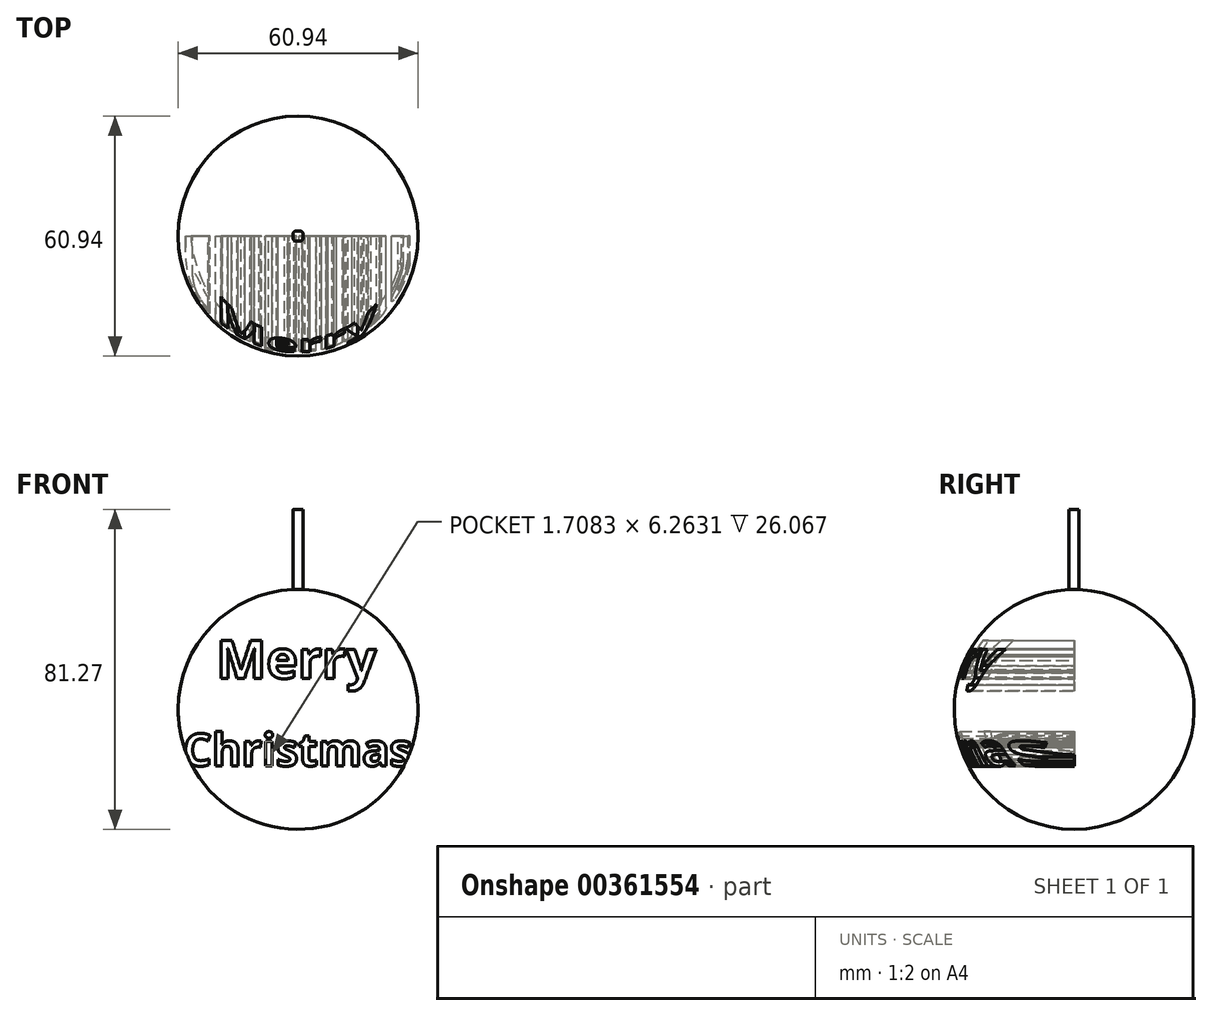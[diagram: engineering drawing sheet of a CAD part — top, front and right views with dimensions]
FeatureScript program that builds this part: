
annotation { "Feature Type Name" : "Feature", "Feature Type Description" : "" }
export const myFeature = defineFeature(function(context is Context, id is Id, definition is map)
    precondition{}
    {
        {
            var Q0;
            Q0=qCreatedBy(makeId("Front.planeOp"),FACE);
            var sketch = newSketch(context, id + "F0", { "sketchPlane" : qUnion([Q0])});
            skCircle(sketch, "E0", {"center": v(0, 0) * mm, "radius": 30.47 * mm});
            skLineSegment(sketch, "E1", {"start": v(-30.47, 0) * mm, "end": v(30.47, 0) * mm});
            skSolve(sketch);
        }
        {
            var Q0;
            {var subQ0=sQuery(id+"F0.wireOp",EDGE,"E1");Q0=makeQuery(id+"F0.imprint","IMPRINT",FACE,{"disambiguationData":[TD([[makeQuery(id+"F0.imprint","IMPRINT",EDGE,{"derivedFrom":subQ0}),-1.0]])]});}
            var Q1;
            Q1=sQuery(id+"F0.wireOp",EDGE,"E1");
            revolve(context, id + "F1", {"entities" : qUnion([Q0]), "axis" : qUnion([Q1]), "revolveType" : RevolveType.FULL});
        }
        {
            var Q0;
            Q0=qCreatedBy(makeId("Top.planeOp"),FACE);
            var sketch = newSketch(context, id + "F2", { "sketchPlane" : qUnion([Q0])});
            skLineSegment(sketch, "E2.bottom", {"start": v(-1.27, 1.27) * mm, "end": v(1.27, 1.27) * mm});
            skLineSegment(sketch, "E2.top", {"start": v(-1.27, -1.27) * mm, "end": v(1.27, -1.27) * mm});
            skLineSegment(sketch, "E2.left", {"start": v(-1.27, 1.27) * mm, "end": v(-1.27, -1.27) * mm});
            skLineSegment(sketch, "E2.right", {"start": v(1.27, 1.27) * mm, "end": v(1.27, -1.27) * mm});
            skSolve(sketch);
        }
        {
            var Q0;
            Q0 = qSketchRegion(id + "F2", true);
            extrude(context, id + "F3", {"entities" : qUnion([Q0]), "operationType" : NewBodyOperationType.ADD, "depth" : 50.8 * mm});
        }
        {
            var Q0;
            {var subQ0=sQuery(id+"F2.wireOp",EDGE,"E2.bottom");var subQ1=sQuery(id+"F2.wireOp",EDGE,"E2.left");Q0=makeQuery(id+"F3.boolean.opBoolean","SPLIT",EDGE,{"disambiguationData":[TD([makeQuery(id+"F3.opExtrude","CAP_FACE",FACE,{"disambiguationData":[OSD([subQ0,sQuery(id+"F2.wireOp",EDGE,"E2.top"),subQ1,sQuery(id+"F2.wireOp",EDGE,"E2.right")])],"isStart":true})])],"derivedFrom":makeQuery(id+"F3.opExtrude","SWEPT_EDGE",EDGE,{"disambiguationData":[OSD([subQ0,subQ1])]})});}
            var Q1;
            {var subQ0=sQuery(id+"F2.wireOp",EDGE,"E2.bottom");var subQ1=sQuery(id+"F2.wireOp",EDGE,"E2.right");Q1=makeQuery(id+"F3.boolean.opBoolean","SPLIT",EDGE,{"disambiguationData":[TD([makeQuery(id+"F3.opExtrude","CAP_FACE",FACE,{"disambiguationData":[OSD([subQ0,sQuery(id+"F2.wireOp",EDGE,"E2.top"),sQuery(id+"F2.wireOp",EDGE,"E2.left"),subQ1])],"isStart":true})])],"derivedFrom":makeQuery(id+"F3.opExtrude","SWEPT_EDGE",EDGE,{"disambiguationData":[OSD([subQ0,subQ1])]})});}
            var Q2;
            {var subQ0=sQuery(id+"F2.wireOp",EDGE,"E2.left");var subQ1=sQuery(id+"F2.wireOp",EDGE,"E2.top");Q2=makeQuery(id+"F3.boolean.opBoolean","SPLIT",EDGE,{"disambiguationData":[TD([makeQuery(id+"F3.opExtrude","CAP_FACE",FACE,{"disambiguationData":[OSD([sQuery(id+"F2.wireOp",EDGE,"E2.bottom"),subQ1,subQ0,sQuery(id+"F2.wireOp",EDGE,"E2.right")])],"isStart":true})])],"derivedFrom":makeQuery(id+"F3.opExtrude","SWEPT_EDGE",EDGE,{"disambiguationData":[OSD([subQ1,subQ0])]})});}
            var Q3;
            {var subQ0=sQuery(id+"F2.wireOp",EDGE,"E2.right");var subQ1=sQuery(id+"F2.wireOp",EDGE,"E2.top");Q3=makeQuery(id+"F3.boolean.opBoolean","SPLIT",EDGE,{"disambiguationData":[TD([makeQuery(id+"F3.opExtrude","CAP_FACE",FACE,{"disambiguationData":[OSD([sQuery(id+"F2.wireOp",EDGE,"E2.bottom"),subQ1,sQuery(id+"F2.wireOp",EDGE,"E2.left"),subQ0])],"isStart":true})])],"derivedFrom":makeQuery(id+"F3.opExtrude","SWEPT_EDGE",EDGE,{"disambiguationData":[OSD([subQ1,subQ0])]})});}
            fillet(context, id + "F4", {"entities" : qUnion([Q0, Q1, Q2, Q3]), "radius" : 0.76 * mm, "tangentPropagation" : true, "allowEdgeOverflow" : false});
        }
        {
            var Q0;
            Q0=qCreatedBy(makeId("Front.planeOp"),FACE);
            var sketch = newSketch(context, id + "F5", { "sketchPlane" : qUnion([Q0])});
            skText(sketch, "E3", { "text": "Merry", "fontName": "OpenSans-Bold.ttf"});
            const initialGuessF5  = {"E3": [-0.02078, 0.0079, 1, 0, 0.00973]};
            skSetInitialGuess(sketch, initialGuessF5);
            skSolve(sketch);
        }
        {
            var Q0;
            Q0 = qSketchRegion(id + "F5", true);
            extrude(context, id + "F6", {"entities" : qUnion([Q0]), "operationType" : NewBodyOperationType.REMOVE, "depth" : 127 * mm});
        }
        {
            var Q0;
            Q0=qCreatedBy(makeId("Front.planeOp"),FACE);
            var sketch = newSketch(context, id + "F7", { "sketchPlane" : qUnion([Q0])});
            skText(sketch, "E4", { "text": "Christmas", "fontName": "OpenSans-Bold.ttf"});
            const initialGuessF7  = {"E4": [-0.02921, -0.01435, 1, 0, 0.00826]};
            skSetInitialGuess(sketch, initialGuessF7);
            skSolve(sketch);
        }
        {
            var Q0;
            Q0 = qSketchRegion(id + "F7", true);
            extrude(context, id + "F8", {"entities" : qUnion([Q0]), "operationType" : NewBodyOperationType.REMOVE, "depth" : 50.8 * mm});
        }
    });
